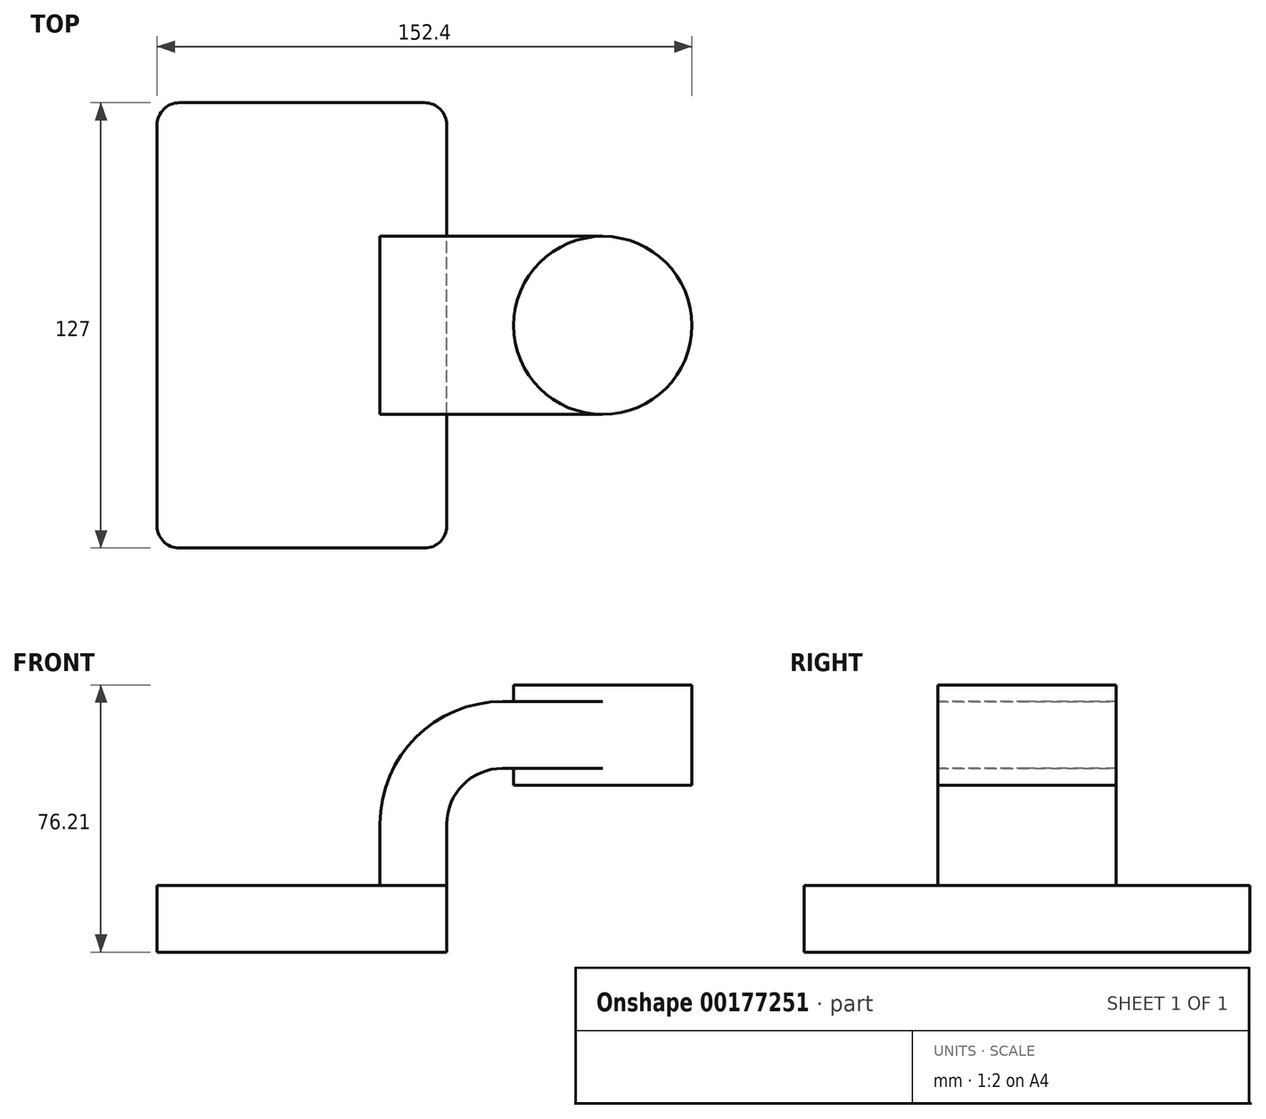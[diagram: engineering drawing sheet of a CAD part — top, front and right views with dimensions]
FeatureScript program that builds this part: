
annotation { "Feature Type Name" : "Feature", "Feature Type Description" : "" }
export const myFeature = defineFeature(function(context is Context, id is Id, definition is map)
    precondition{}
    {
        {
            var Q0;
            Q0=qCreatedBy(makeId("Front.planeOp"),FACE);
            var sketch = newSketch(context, id + "F0", { "sketchPlane" : qUnion([Q0])});
            skLineSegment(sketch, "E0.bottom", {"start": v(41.28, -9.52) * mm, "end": v(-41.28, -9.53) * mm});
            skLineSegment(sketch, "E0.top", {"start": v(41.27, 9.53) * mm, "end": v(-41.28, 9.53) * mm});
            skLineSegment(sketch, "E0.left", {"start": v(41.28, -9.53) * mm, "end": v(41.28, 9.53) * mm});
            skLineSegment(sketch, "E0.right", {"start": v(-41.28, -9.53) * mm, "end": v(-41.28, 9.53) * mm});
            skPoint(sketch, "E0.middle", {"position": v(0, 0) * mm});
            skLineSegment(sketch, "E1.bottom", {"start": v(111.12, 38.1) * mm, "end": v(60.32, 38.1) * mm});
            skLineSegment(sketch, "E1.top", {"start": v(111.12, 66.68) * mm, "end": v(60.32, 66.68) * mm});
            skLineSegment(sketch, "E1.left", {"start": v(111.12, 38.1) * mm, "end": v(111.12, 66.68) * mm});
            skLineSegment(sketch, "E1.right", {"start": v(60.32, 38.1) * mm, "end": v(60.32, 66.67) * mm});
            skPoint(sketch, "E1.middle", {"position": v(85.72, 52.39) * mm});
            skLineSegment(sketch, "E2", {"start": v(41.27, 9.53) * mm, "end": v(41.27, 27) * mm});
            skArc(sketch, "E3", {"start": v(41.27, 27) * mm, "mid": v(45.92, 38.23) * mm, "end": v(57.15, 42.88) * mm});
            skLineSegment(sketch, "E4", {"start": v(57.15, 42.88) * mm, "end": v(85.73, 42.88) * mm});
            skLineSegment(sketch, "E5.0", {"start": v(57.15, 61.93) * mm, "end": v(85.73, 61.93) * mm});
            skArc(sketch, "E5.1", {"start": v(22.23, 27) * mm, "mid": v(32.45, 51.7) * mm, "end": v(57.15, 61.93) * mm});
            skLineSegment(sketch, "E5.2", {"start": v(22.23, 9.53) * mm, "end": v(22.23, 27) * mm});
            skLineSegment(sketch, "E6", {"start": v(85.72, 38.1) * mm, "end": v(85.72, 66.68) * mm});
            skFitSpline(sketch, "E7", {"points": [v(-41.28, 9.53) * mm, v(57.15, 61.93) * mm], "startDerivative": vector(2.2, 118.76) * mm, "endDerivative": vector(151.86, -0.74) * mm});
            skSolve(sketch);
        }
        {
            var Q0;
            Q0=makeQuery(id+"F0.imprint","IMPRINT",FACE,{"disambiguationData":[TD([[makeQuery(id+"F0.imprint","IMPRINT",EDGE,{"derivedFrom":sQuery(id+"F0.wireOp",EDGE,"E0.bottom")}),-1.0]])]});
            extrude(context, id + "F1", {"entities" : qUnion([Q0]), "endBound" : BoundingType.SYMMETRIC, "depth" : 127 * mm});
        }
        {
            var Q0;
            Q0=makeQuery(id+"F0.imprint","IMPRINT",FACE,{"disambiguationData":[TD([[makeQuery(id+"F0.imprint","IMPRINT",EDGE,{"derivedFrom":sQuery(id+"F0.wireOp",EDGE,"E5.1")}),1.0]])]});
            extrude(context, id + "F2", {"entities" : qUnion([Q0]), "endBound" : BoundingType.SYMMETRIC, "depth" : 15.88 * mm});
        }
        {
            var Q0;
            {var subQ1=sQuery(id+"F0.wireOp",EDGE,"E2");Q0=makeQuery(id+"F0.imprint","IMPRINT",FACE,{"disambiguationData":[TD([[makeQuery(id+"F0.imprint","IMPRINT",EDGE,{"derivedFrom":subQ1}),1.0]])]});}
            var Q1;
            {var subQ0=sQuery(id+"F0.wireOp",EDGE,"E4");var subQ1=sQuery(id+"F0.wireOp",EDGE,"E1.right");var subQ2=makeQuery(id+"F0.imprint","INTERSECT",VERTEX,{"derivedFrom":[subQ1,subQ0]});Q1=makeQuery(id+"F0.imprint","IMPRINT",FACE,{"disambiguationData":[TD([[makeQuery(id+"F0.imprint","IMPRINT",EDGE,{"disambiguationData":[TD([[subQ2,-1.0]])],"derivedFrom":subQ1}),-1.0]])]});}
            extrude(context, id + "F3", {"entities" : qUnion([Q0, Q1]), "endBound" : BoundingType.SYMMETRIC, "depth" : 50.8 * mm});
        }
        {
            var Q0;
            {var subQ0=sQuery(id+"F0.wireOp",EDGE,"E1.left");Q0=makeQuery(id+"F0.imprint","IMPRINT",FACE,{"disambiguationData":[TD([[makeQuery(id+"F0.imprint","IMPRINT",EDGE,{"derivedFrom":subQ0}),1.0]])]});}
            var Q1;
            Q1=sQuery(id+"F0.wireOp",EDGE,"E6");
            revolve(context, id + "F4", {"operationType" : NewBodyOperationType.ADD, "entities" : qUnion([Q0]), "axis" : qUnion([Q1]), "revolveType" : RevolveType.FULL});
        }
        {
            var Q0;
            Q0=makeQuery(id+"F1.opExtrude","CAP_EDGE",EDGE,{"disambiguationData":[OSD([sQuery(id+"F0.wireOp",EDGE,"E0.left")])],"isStart":false});
            var Q1;
            Q1=makeQuery(id+"F1.opExtrude","CAP_EDGE",EDGE,{"disambiguationData":[OSD([sQuery(id+"F0.wireOp",EDGE,"E0.right")])],"isStart":false});
            var Q2;
            Q2=makeQuery(id+"F1.opExtrude","CAP_EDGE",EDGE,{"disambiguationData":[OSD([sQuery(id+"F0.wireOp",EDGE,"E0.left")])],"isStart":true});
            var Q3;
            Q3=makeQuery(id+"F1.opExtrude","CAP_EDGE",EDGE,{"disambiguationData":[OSD([sQuery(id+"F0.wireOp",EDGE,"E0.right")])],"isStart":true});
            fillet(context, id + "F5", {"entities" : qUnion([Q0, Q1, Q2, Q3]), "radius" : 6.35 * mm, "tangentPropagation" : true, "allowEdgeOverflow" : false});
        }
    });
